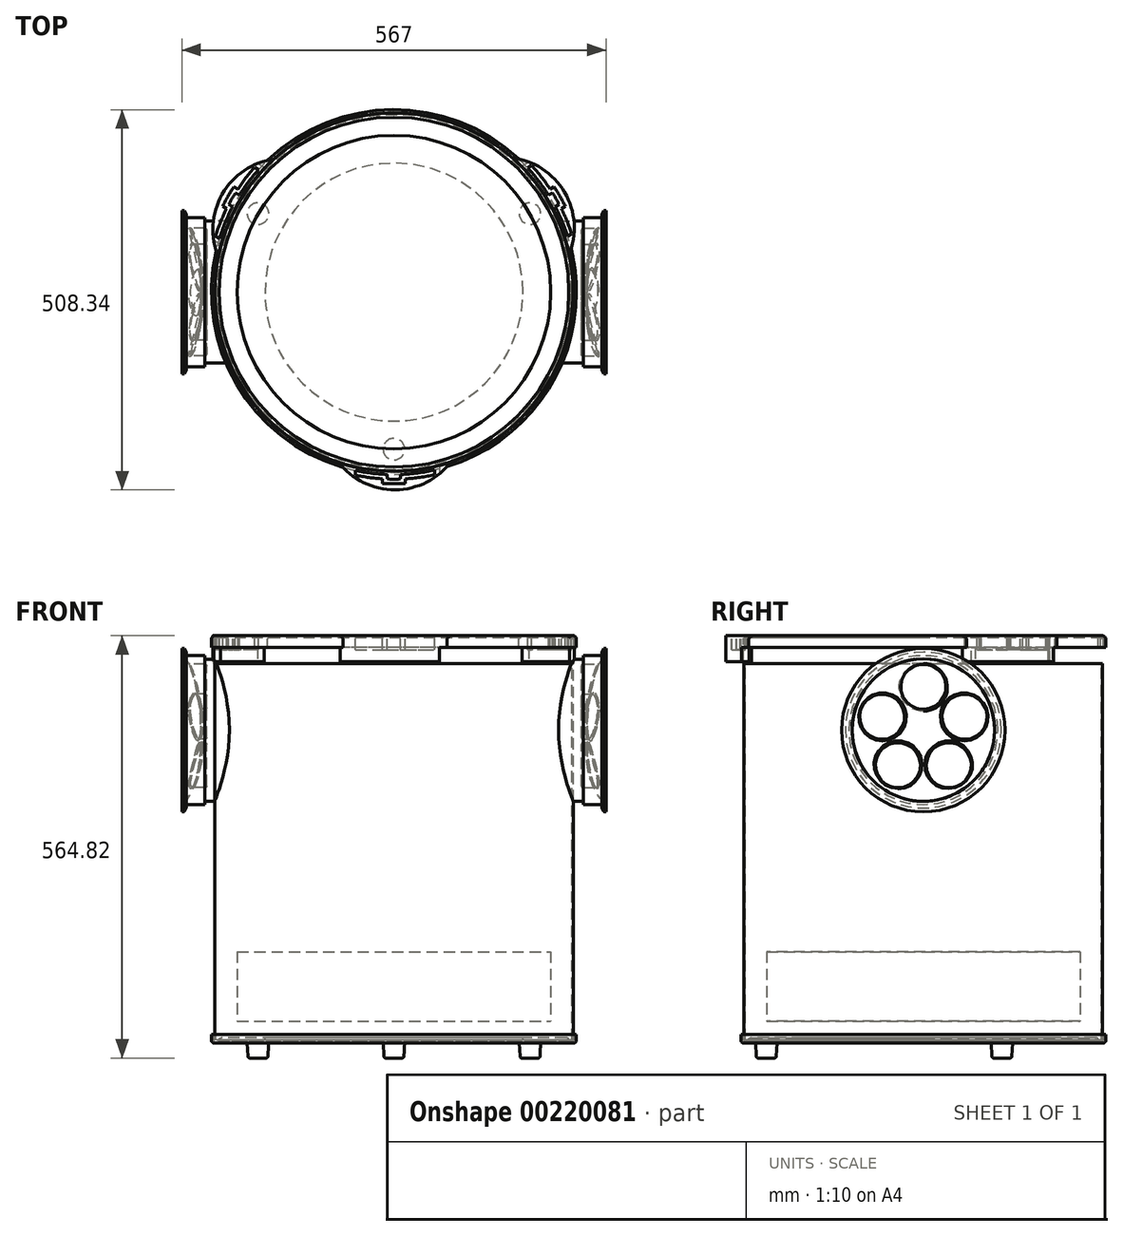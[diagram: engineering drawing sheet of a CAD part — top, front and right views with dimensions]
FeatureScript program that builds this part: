
annotation { "Feature Type Name" : "Feature", "Feature Type Description" : "" }
export const myFeature = defineFeature(function(context is Context, id is Id, definition is map)
    precondition{}
    {
        {
            var Q0;
            Q0=qCreatedBy(makeId("Front.planeOp"),FACE);
            var sketch = newSketch(context, id + "F0", { "sketchPlane" : qUnion([Q0])});
            skLineSegment(sketch, "E0", {"start": v(0, 0) * mm, "end": v(266.4, 0) * mm, "construction": true});
            skArc(sketch, "E1", {"start": v(244, 0) * mm, "mid": v(238.93, 5.08) * mm, "end": v(233.85, 0) * mm});
            skLineSegment(sketch, "E2", {"start": v(233.85, 0) * mm, "end": v(233.85, -10.92) * mm});
            skLineSegment(sketch, "E3", {"start": v(244, 0) * mm, "end": v(244, -10.92) * mm});
            skArc(sketch, "E4", {"start": v(240.83, 0) * mm, "mid": v(238.93, 1.9) * mm, "end": v(237.02, 0) * mm});
            skLineSegment(sketch, "E5", {"start": v(237.02, 0) * mm, "end": v(237.02, -10.92) * mm});
            skLineSegment(sketch, "E6", {"start": v(240.83, 0) * mm, "end": v(240.83, -10.92) * mm});
            skLineSegment(sketch, "E7", {"start": v(233.85, -10.92) * mm, "end": v(237.02, -10.92) * mm});
            skLineSegment(sketch, "E8.trimOffspring", {"start": v(240.83, -10.92) * mm, "end": v(244, -10.92) * mm});
            skLineSegment(sketch, "E9", {"start": v(239.69, 0) * mm, "end": v(239.69, -535.86) * mm});
            skLineSegment(sketch, "E10", {"start": v(238.16, 0) * mm, "end": v(238.16, -535.86) * mm});
            skLineSegment(sketch, "E11", {"start": v(238.16, 0) * mm, "end": v(239.69, 0) * mm});
            skLineSegment(sketch, "E12", {"start": v(-59.24, -539.93) * mm, "end": v(313.45, -539.93) * mm, "construction": true});
            skLineSegment(sketch, "E13", {"start": v(244, -528.24) * mm, "end": v(244, -535.86) * mm});
            skLineSegment(sketch, "E14", {"start": v(0, 0) * mm, "end": v(0, -616.75) * mm, "construction": true});
            skLineSegment(sketch, "E15", {"start": v(240.83, -528.24) * mm, "end": v(244, -528.24) * mm});
            skLineSegment(sketch, "E16", {"start": v(240.83, -528.24) * mm, "end": v(240.83, -536) * mm});
            skLineSegment(sketch, "E17", {"start": v(235.18, -536.75) * mm, "end": v(240.07, -536.75) * mm});
            skLineSegment(sketch, "E18", {"start": v(230.42, -532.69) * mm, "end": v(172.5, -532.69) * mm});
            skLineSegment(sketch, "E19", {"start": v(172.5, -535.86) * mm, "end": v(230.6, -535.86) * mm});
            skLineSegment(sketch, "E20", {"start": v(235.37, -539.93) * mm, "end": v(239.94, -539.93) * mm});
            skLineSegment(sketch, "E21", {"start": v(238.16, -535.86) * mm, "end": v(239.69, -535.86) * mm});
            skLineSegment(sketch, "E22", {"start": v(172.5, -532.69) * mm, "end": v(172.5, -535.86) * mm});
            skArc(sketch, "E23.filletArc", {"start": v(231.36, -536.5) * mm, "mid": v(232.73, -538.96) * mm, "end": v(235.37, -539.93) * mm});
            skPoint(sketch, "E24.visualSharp", {"position": v(244, -539.93) * mm});
            skArc(sketch, "E24.filletArc", {"start": v(239.94, -539.93) * mm, "mid": v(242.81, -538.74) * mm, "end": v(244, -535.86) * mm});
            skPoint(sketch, "E25.visualSharp", {"position": v(231.3, -535.86) * mm});
            skPoint(sketch, "E26.visualSharp", {"position": v(234.48, -532.69) * mm});
            skArc(sketch, "E26.filletArc", {"start": v(234.43, -536.11) * mm, "mid": v(233.05, -533.66) * mm, "end": v(230.42, -532.69) * mm});
            skPoint(sketch, "E27.visualSharp", {"position": v(234.48, -536.75) * mm});
            skPoint(sketch, "E28.visualSharp", {"position": v(240.83, -536.75) * mm});
            skArc(sketch, "E28.filletArc", {"start": v(240.07, -536.75) * mm, "mid": v(240.6, -536.53) * mm, "end": v(240.83, -536) * mm});
            skArc(sketch, "E29.filletArc", {"start": v(231.36, -536.5) * mm, "mid": v(231.1, -536.05) * mm, "end": v(230.6, -535.86) * mm});
            skArc(sketch, "E30.filletArc", {"start": v(234.43, -536.11) * mm, "mid": v(234.69, -536.57) * mm, "end": v(235.18, -536.75) * mm});
            skPoint(sketch, "E31", {"position": v(238.93, 5.08) * mm});
            skSolve(sketch);
        }
        {
            var Q0;
            Q0=qCreatedBy(makeId("Front.planeOp"),FACE);
            var sketch = newSketch(context, id + "F1", { "sketchPlane" : qUnion([Q0])});
            skLineSegment(sketch, "E32", {"start": v(0, 0) * mm, "end": v(0, -692.69) * mm, "construction": true});
            skSolve(sketch);
        }
        {
            var Q0;
            Q0 = qSketchRegion(id + "F0", true);
            var Q1;
            Q1 = qConstructionFilter(qBodyType(qCreatedBy(id + "F0" ,EDGE), BodyType.WIRE), ConstructionObject.NO);
            var Q2;
            Q2=sQuery(id+"F1.wireOp",EDGE,"E32");
            revolve(context, id + "F2", {"entities" : qUnion([Q0]), "surfaceEntities" : qUnion([Q1]), "axis" : qUnion([Q2]), "revolveType" : RevolveType.FULL});
        }
        {
            var Q0;
            Q0=qCreatedBy(makeId("Right.planeOp"),FACE);
            cPlane(context, id + "F3", {"entities" : qUnion([Q0]), "cplaneType" : CPlaneType.OFFSET, "offset" : 283.5 * mm, "width" : 152.4 * mm, "height" : 152.4 * mm});
        }
        {
            var Q0;
            Q0=qCreatedBy(id+"F3.planeOp",FACE);
            cPlane(context, id + "F4", {"entities" : qUnion([Q0]), "cplaneType" : CPlaneType.OFFSET, "offset" : 5.6 * mm, "oppositeDirection" : true, "width" : 152.4 * mm, "height" : 152.4 * mm});
        }
        {
            var Q0;
            Q0=qCreatedBy(id+"F4.planeOp",FACE);
            cPlane(context, id + "F5", {"entities" : qUnion([Q0]), "cplaneType" : CPlaneType.OFFSET, "offset" : 24.76 * mm, "oppositeDirection" : true, "width" : 152.4 * mm, "height" : 152.4 * mm});
        }
        {
            var Q0;
            Q0=qCreatedBy(id+"F3.planeOp",FACE);
            var sketch = newSketch(context, id + "F6", { "sketchPlane" : qUnion([Q0])});
            skLineSegment(sketch, "E33", {"start": v(0, 0) * mm, "end": v(0, -1376.22) * mm, "construction": true});
            skCircle(sketch, "E34", {"center": v(0, -121.28) * mm, "radius": 109.22 * mm});
            skCircle(sketch, "E35", {"center": v(0, -121.28) * mm, "radius": 99.57 * mm});
            skCircle(sketch, "E36", {"center": v(0, -121.28) * mm, "radius": 95 * mm});
            skLineSegment(sketch, "E37", {"start": v(-238.93, 5.08) * mm, "end": v(238.93, 5.08) * mm, "construction": true});
            skSolve(sketch);
        }
        {
            var Q0;
            Q0=makeQuery(id+"F6.imprint","IMPRINT",FACE,{"disambiguationData":[TD([[makeQuery(id+"F6.imprint","IMPRINT",EDGE,{"derivedFrom":sQuery(id+"F6.wireOp",EDGE,"E36")}),1.0]])]});
            var Q1;
            Q1=sQuery(id+"F6.wireOp",EDGE,"E37");
            var Q2;
            Q2=sQuery(id+"F6.wireOp",EDGE,"E36");
            var Q3;
            Q3=makeQuery(id+"F2.opRevolve","SWEPT_FACE",FACE,{"disambiguationData":[OSD([sQuery(id+"F0.wireOp",EDGE,"E9")])]});
            extrude(context, id + "F7", {"entities" : qUnion([Q0]), "surfaceEntities" : qUnion([Q1, Q2]), "endBound" : BoundingType.UP_TO_SURFACE, "oppositeDirection" : true, "endBoundEntityFace" : qUnion([Q3]), "depth" : 25.4 * mm});
        }
        {
            var Q0;
            Q0=makeQuery(id+"F6.imprint","IMPRINT",FACE,{"disambiguationData":[TD([[makeQuery(id+"F6.imprint","IMPRINT",EDGE,{"derivedFrom":sQuery(id+"F6.wireOp",EDGE,"E35")}),1.0]])]});
            var Q1;
            Q1=qCreatedBy(id+"F5.planeOp",FACE);
            extrude(context, id + "F8", {"entities" : qUnion([Q0]), "operationType" : NewBodyOperationType.ADD, "endBound" : BoundingType.UP_TO_SURFACE, "oppositeDirection" : true, "endBoundEntityFace" : qUnion([Q1]), "depth" : 25.4 * mm});
        }
        {
            var Q0;
            Q0=makeQuery(id+"F6.imprint","IMPRINT",FACE,{"disambiguationData":[TD([[makeQuery(id+"F6.imprint","IMPRINT",EDGE,{"derivedFrom":sQuery(id+"F6.wireOp",EDGE,"E34")}),1.0]])]});
            var Q1;
            Q1=qCreatedBy(id+"F4.planeOp",FACE);
            extrude(context, id + "F9", {"entities" : qUnion([Q0]), "operationType" : NewBodyOperationType.ADD, "endBound" : BoundingType.UP_TO_SURFACE, "oppositeDirection" : true, "endBoundEntityFace" : qUnion([Q1]), "depth" : 25.4 * mm});
        }
        {
            var Q0;
            Q0=qCreatedBy(makeId("Front.planeOp"),FACE);
            var sketch = newSketch(context, id + "F10", { "sketchPlane" : qUnion([Q0])});
            skLineSegment(sketch, "E38.0", {"start": v(283.5, -12.06) * mm, "end": v(283.5, -26.03) * mm, "construction": true});
            skPoint(sketch, "E39", {"position": v(283.5, -26.03) * mm});
            skPoint(sketch, "E40.orphan", {"position": v(283.5, -121.28) * mm});
            skPoint(sketch, "E41", {"position": v(257.34, -121.28) * mm});
            skEllipticalArc(sketch, "E42", {});
            skLineSegment(sketch, "E43", {"start": v(283.5, -26.03) * mm, "end": v(283.5, -121.28) * mm});
            skLineSegment(sketch, "E44", {"start": v(283.5, -121.28) * mm, "end": v(257.34, -121.28) * mm});
            skPoint(sketch, "E45.trimOffspring.end.orphan", {"position": v(283.5, -230.5) * mm});
            const initialGuessF10  = {"E42": [0.28350210000000003, -0.121285, 0, 1, 0.09525, 0.026162, 0, 1.5707963267948966]};
            skSetInitialGuess(sketch, initialGuessF10);
            skSolve(sketch);
        }
        {
            var Q0;
            Q0 = qSketchRegion(id + "F10", true);
            var Q1;
            Q1=makeQuery(id+"F7.opExtrude","SWEPT_FACE",FACE,{"disambiguationData":[OSD([sQuery(id+"F6.wireOp",EDGE,"E36")])]});
            revolve(context, id + "F11", {"operationType" : NewBodyOperationType.REMOVE, "entities" : qUnion([Q0]), "axis" : qUnion([Q1]), "revolveType" : RevolveType.FULL, "oppositeDirection" : true});
        }
        {
            var Q0;
            Q0=qCreatedBy(id+"F3.planeOp",FACE);
            var sketch = newSketch(context, id + "F12", { "sketchPlane" : qUnion([Q0])});
            skCircle(sketch, "E46.0", {"center": v(0, -121.28) * mm, "radius": 95.25 * mm, "construction": true});
            skLineSegment(sketch, "E47", {"start": v(0, -121.28) * mm, "end": v(0, 34.17) * mm, "construction": true});
            skCircle(sketch, "E48", {"center": v(0, -63.3) * mm, "radius": 30.16 * mm});
            skCircle(sketch, "E49.0", {"center": v(0, -121.28) * mm, "radius": 109.22 * mm, "construction": true});
            skCircle(sketch, "E50.1.0", {"center": v(-55.14, -103.37) * mm, "radius": 30.16 * mm});
            skCircle(sketch, "E50.2.0", {"center": v(-34.08, -168.19) * mm, "radius": 30.16 * mm});
            skCircle(sketch, "E50.3.0", {"center": v(34.08, -168.19) * mm, "radius": 30.16 * mm});
            skCircle(sketch, "E50.4.0", {"center": v(55.14, -103.37) * mm, "radius": 30.16 * mm});
            skSolve(sketch);
        }
        {
            var Q0;
            Q0 = qSketchRegion(id + "F12", true);
            extrude(context, id + "F13", {"entities" : qUnion([Q0]), "operationType" : NewBodyOperationType.REMOVE, "oppositeDirection" : true, "depth" : 33.02 * mm});
        }
        {
            var Q0;
            Q0=makeQuery(id+"F13.boolean.opBoolean","COPY",EDGE,{"derivedFrom":makeQuery(id+"F13.opExtrude","CAP_EDGE",EDGE,{"disambiguationData":[OSD([sQuery(id+"F12.wireOp",EDGE,"E50.3.0")])],"isStart":false})});
            var Q1;
            Q1=makeQuery(id+"F13.boolean.opBoolean","COPY",EDGE,{"derivedFrom":makeQuery(id+"F13.opExtrude","CAP_EDGE",EDGE,{"disambiguationData":[OSD([sQuery(id+"F12.wireOp",EDGE,"E50.4.0")])],"isStart":false})});
            var Q2;
            Q2=makeQuery(id+"F13.boolean.opBoolean","COPY",FACE,{"derivedFrom":makeQuery(id+"F13.opExtrude","SWEPT_FACE",FACE,{"disambiguationData":[OSD([sQuery(id+"F12.wireOp",EDGE,"E48")])]})});
            var Q3;
            Q3=makeQuery(id+"F13.boolean.opBoolean","COPY",EDGE,{"derivedFrom":makeQuery(id+"F13.opExtrude","CAP_EDGE",EDGE,{"disambiguationData":[OSD([sQuery(id+"F12.wireOp",EDGE,"E50.1.0")])],"isStart":false})});
            var Q4;
            Q4=makeQuery(id+"F13.boolean.opBoolean","COPY",EDGE,{"derivedFrom":makeQuery(id+"F13.opExtrude","CAP_EDGE",EDGE,{"disambiguationData":[OSD([sQuery(id+"F12.wireOp",EDGE,"E50.2.0")])],"isStart":false})});
            var Q5;
            Q5=makeQuery(id+"F13.boolean.opBoolean","INTERSECT",EDGE,{"derivedFrom":[makeQuery(id+"F11.boolean.opBoolean","COPY",FACE,{"derivedFrom":makeQuery(id+"F11.opRevolve","SWEPT_FACE",FACE,{"disambiguationData":[OSD([sQuery(id+"F10.wireOp",EDGE,"E42")])]})}),makeQuery(id+"F13.opExtrude","SWEPT_FACE",FACE,{"disambiguationData":[OSD([sQuery(id+"F12.wireOp",EDGE,"E50.4.0")])]})]});
            var Q6;
            Q6=makeQuery(id+"F13.boolean.opBoolean","INTERSECT",EDGE,{"derivedFrom":[makeQuery(id+"F11.boolean.opBoolean","COPY",FACE,{"derivedFrom":makeQuery(id+"F11.opRevolve","SWEPT_FACE",FACE,{"disambiguationData":[OSD([sQuery(id+"F10.wireOp",EDGE,"E42")])]})}),makeQuery(id+"F13.opExtrude","SWEPT_FACE",FACE,{"disambiguationData":[OSD([sQuery(id+"F12.wireOp",EDGE,"E50.3.0")])]})]});
            var Q7;
            Q7=makeQuery(id+"F13.boolean.opBoolean","INTERSECT",EDGE,{"derivedFrom":[makeQuery(id+"F11.boolean.opBoolean","COPY",FACE,{"derivedFrom":makeQuery(id+"F11.opRevolve","SWEPT_FACE",FACE,{"disambiguationData":[OSD([sQuery(id+"F10.wireOp",EDGE,"E42")])]})}),makeQuery(id+"F13.opExtrude","SWEPT_FACE",FACE,{"disambiguationData":[OSD([sQuery(id+"F12.wireOp",EDGE,"E50.2.0")])]})]});
            var Q8;
            Q8=makeQuery(id+"F13.boolean.opBoolean","INTERSECT",EDGE,{"derivedFrom":[makeQuery(id+"F11.boolean.opBoolean","COPY",FACE,{"derivedFrom":makeQuery(id+"F11.opRevolve","SWEPT_FACE",FACE,{"disambiguationData":[OSD([sQuery(id+"F10.wireOp",EDGE,"E42")])]})}),makeQuery(id+"F13.opExtrude","SWEPT_FACE",FACE,{"disambiguationData":[OSD([sQuery(id+"F12.wireOp",EDGE,"E50.1.0")])]})]});
            var Q9;
            Q9=makeQuery(id+"F11.boolean.opBoolean","COPY",EDGE,{"derivedFrom":makeQuery(id+"F11.opRevolve","SWEPT_EDGE",EDGE,{"disambiguationData":[OSD([sQuery(id+"F10.wireOp",EDGE,"E42"),sQuery(id+"F10.wireOp",EDGE,"E43")])]})});
            fillet(context, id + "F14", {"entities" : qUnion([Q0, Q1, Q2, Q3, Q4, Q5, Q6, Q7, Q8, Q9]), "radius" : 2.3 * mm, "tangentPropagation" : true, "allowEdgeOverflow" : false});
        }
        {
            var Q0;
            Q0=qCreatedBy(makeId("Front.planeOp"),FACE);
            var sketch = newSketch(context, id + "F15", { "sketchPlane" : qUnion([Q0])});
            skLineSegment(sketch, "E51.0", {"start": v(277.91, -17.14) * mm, "end": v(277.91, -12.06) * mm});
            skLineSegment(sketch, "E52", {"start": v(277.91, -17.14) * mm, "end": v(280.45, -12.06) * mm});
            skLineSegment(sketch, "E53", {"start": v(277.91, -12.06) * mm, "end": v(280.45, -12.06) * mm});
            skPoint(sketch, "E54.orphan", {"position": v(277.91, -230.5) * mm});
            skSolve(sketch);
        }
        {
            var Q0;
            Q0 = qSketchRegion(id + "F15", true);
            var Q1;
            Q1=makeQuery(id+"F9.opExtrude","SWEPT_FACE",FACE,{"disambiguationData":[OSD([sQuery(id+"F6.wireOp",EDGE,"E34")])]});
            revolve(context, id + "F16", {"operationType" : NewBodyOperationType.REMOVE, "entities" : qUnion([Q0]), "axis" : qUnion([Q1]), "revolveType" : RevolveType.FULL, "oppositeDirection" : true});
        }
        {
            var Q0;
            Q0=makeQuery(id+"F7.opExtrude","SWEPT_BODY",BODY,{"disambiguationData":[OSD([sQuery(id+"F6.wireOp",EDGE,"E36")])]});
            var Q1;
            Q1=qCreatedBy(makeId("Right.planeOp"),FACE);
            mirror(context, id + "F17", {"entities" : qUnion([Q0]), "mirrorPlane" : qUnion([Q1])});
        }
        {
            var Q0;
            Q0=makeQuery(id+"F2.opRevolve","SWEPT_FACE",FACE,{"disambiguationData":[OSD([sQuery(id+"F0.wireOp",EDGE,"E19")])]});
            cPlane(context, id + "F18", {"entities" : qUnion([Q0]), "cplaneType" : CPlaneType.OFFSET, "offset" : 25.4 * mm, "oppositeDirection" : true, "width" : 152.4 * mm, "height" : 152.4 * mm});
        }
        {
            var Q0;
            Q0=qCreatedBy(id+"F18.planeOp",FACE);
            var sketch = newSketch(context, id + "F19", { "sketchPlane" : qUnion([Q0])});
            skCircle(sketch, "E55.0", {"center": v(0, 0) * mm, "radius": 172.5 * mm, "construction": true});
            skCircle(sketch, "E56", {"center": v(0, 0) * mm, "radius": 209.55 * mm});
            skSolve(sketch);
        }
        {
            var Q0;
            Q0 = qSketchRegion(id + "F19", true);
            extrude(context, id + "F20", {"entities" : qUnion([Q0]), "oppositeDirection" : true, "depth" : 92.96 * mm});
        }
        {
            var Q0;
            Q0=makeQuery(id+"F2.opRevolve","SWEPT_FACE",FACE,{"disambiguationData":[OSD([sQuery(id+"F0.wireOp",EDGE,"E19")])]});
            var sketch = newSketch(context, id + "F21", { "sketchPlane" : qUnion([Q0])});
            skCircle(sketch, "E57.0", {"center": v(0, 0) * mm, "radius": 244 * mm, "construction": true});
            skCircle(sketch, "E58", {"center": v(0, 0) * mm, "radius": 209.97 * mm, "construction": true});
            skCircle(sketch, "E59", {"center": v(0, 209.97) * mm, "radius": 14.48 * mm});
            skCircle(sketch, "E60.1.0", {"center": v(-181.84, -104.98) * mm, "radius": 14.48 * mm});
            skCircle(sketch, "E60.2.0", {"center": v(181.84, -104.98) * mm, "radius": 14.48 * mm});
            skSolve(sketch);
        }
        {
            var Q0;
            Q0 = qSketchRegion(id + "F21", true);
            extrude(context, id + "F22", {"entities" : qUnion([Q0]), "operationType" : NewBodyOperationType.ADD, "depth" : 23.88 * mm, "hasDraft" : true, "draftAngle" : 3 * degree, "draftPullDirection" : true});
        }
        {
            var Q0;
            Q0=makeQuery(id+"F22.opExtrude","CAP_EDGE",EDGE,{"disambiguationData":[OSD([sQuery(id+"F21.wireOp",EDGE,"E59")])],"isStart":false});
            var Q1;
            Q1=makeQuery(id+"F22.opExtrude","CAP_EDGE",EDGE,{"disambiguationData":[OSD([sQuery(id+"F21.wireOp",EDGE,"E60.1.0")])],"isStart":false});
            var Q2;
            Q2=makeQuery(id+"F22.opExtrude","CAP_EDGE",EDGE,{"disambiguationData":[OSD([sQuery(id+"F21.wireOp",EDGE,"E60.2.0")])],"isStart":false});
            fillet(context, id + "F23", {"entities" : qUnion([Q0, Q1, Q2]), "radius" : 2.3 * mm, "tangentPropagation" : true, "allowEdgeOverflow" : false});
        }
        {
            var Q0;
            Q0=qCreatedBy(makeId("Top.planeOp"),FACE);
            cPlane(context, id + "F24", {"entities" : qUnion([Q0]), "cplaneType" : CPlaneType.OFFSET, "offset" : 5.08 * mm, "width" : 152.4 * mm, "height" : 152.4 * mm});
        }
        {
            var Q0;
            Q0=qCreatedBy(id+"F24.planeOp",FACE);
            var sketch = newSketch(context, id + "F25", { "sketchPlane" : qUnion([Q0])});
            skCircle(sketch, "E61.0", {"center": v(0, 0) * mm, "radius": 244 * mm, "construction": true});
            skLineSegment(sketch, "E62", {"start": v(0, 0) * mm, "end": v(0, -355.56) * mm, "construction": true});
            skArc(sketch, "E63", {"start": v(-74.28, -227.08) * mm, "mid": v(1.49, -238.92) * mm, "end": v(77.1, -226.14) * mm});
            skLineSegment(sketch, "E64", {"start": v(-74.28, -176.06) * mm, "end": v(-74.28, -268.16) * mm, "construction": true});
            skLineSegment(sketch, "E65", {"start": v(77.1, -171.77) * mm, "end": v(77.1, -259.18) * mm, "construction": true});
            skPoint(sketch, "E66", {"position": v(0, -264.33) * mm});
            skCircle(sketch, "E67.0", {"center": v(0, 0) * mm, "radius": 233.85 * mm, "construction": true});
            skPoint(sketch, "E68", {"position": v(-74.28, -227.08) * mm});
            skPoint(sketch, "E69", {"position": v(77.1, -226.14) * mm});
            skArc(sketch, "E70", {"start": v(-74.28, -227.08) * mm, "mid": v(1.64, -264.33) * mm, "end": v(77.1, -226.14) * mm});
            skArc(sketch, "E71.1.0", {"start": v(233.8, 49.21) * mm, "mid": v(206.17, 120.75) * mm, "end": v(157.3, 179.84) * mm});
            skArc(sketch, "E71.1.1", {"start": v(233.8, 49.21) * mm, "mid": v(228.1, 133.59) * mm, "end": v(157.3, 179.84) * mm});
            skArc(sketch, "E71.2.0", {"start": v(-159.52, 177.87) * mm, "mid": v(-207.65, 118.17) * mm, "end": v(-234.4, 46.3) * mm});
            skArc(sketch, "E71.2.1", {"start": v(-159.52, 177.87) * mm, "mid": v(-229.74, 130.74) * mm, "end": v(-234.4, 46.3) * mm});
            skSolve(sketch);
        }
        {
            var Q0;
            Q0 = qSketchRegion(id + "F25", true);
            var Q1;
            Q1=makeQuery(id+"F2.opRevolve","SWEPT_FACE",FACE,{"disambiguationData":[OSD([sQuery(id+"F0.wireOp",EDGE,"E8.trimOffspring")])]});
            extrude(context, id + "F26", {"entities" : qUnion([Q0]), "operationType" : NewBodyOperationType.ADD, "oppositeDirection" : true, "endBoundEntityFace" : qUnion([Q1]), "depth" : 35.05 * mm});
        }
        {
            var Q0;
            Q0=makeQuery(id+"F26.opExtrude","CAP_FACE",FACE,{"disambiguationData":[OSD([sQuery(id+"F25.wireOp",EDGE,"E71.2.0"),sQuery(id+"F25.wireOp",EDGE,"E71.2.1")])],"isStart":false});
            var sketch = newSketch(context, id + "F27", { "sketchPlane" : qUnion([Q0])});
            skArc(sketch, "E72.0", {"start": v(-159.52, -177.87) * mm, "mid": v(-171.17, -175.61) * mm, "end": v(-182.44, -171.92) * mm});
            skArc(sketch, "E73.0", {"start": v(-159.52, -177.87) * mm, "mid": v(-165.82, -172.01) * mm, "end": v(-171.91, -165.93) * mm});
            skLineSegment(sketch, "E74", {"start": v(-147.33, -83.85) * mm, "end": v(-229.74, -130.74) * mm, "construction": true});
            skLineSegment(sketch, "E75", {"start": v(-171.91, -165.93) * mm, "end": v(-182.44, -171.92) * mm});
            skLineSegment(sketch, "E76", {"start": v(-230.45, -63.05) * mm, "end": v(-240.99, -69.05) * mm});
            skArc(sketch, "E77.trimOffspring", {"start": v(-240.99, -69.05) * mm, "mid": v(-238.4, -57.47) * mm, "end": v(-234.4, -46.3) * mm});
            skArc(sketch, "E78.trimOffspring", {"start": v(-230.45, -63.05) * mm, "mid": v(-232.58, -54.71) * mm, "end": v(-234.4, -46.3) * mm});
            skPoint(sketch, "E79.orphan", {"position": v(-213.52, -189.6) * mm});
            skArc(sketch, "E80.1.0", {"start": v(233.8, -49.21) * mm, "mid": v(237.67, -60.43) * mm, "end": v(240.1, -72.04) * mm});
            skArc(sketch, "E80.1.1", {"start": v(233.8, -49.21) * mm, "mid": v(231.88, -57.6) * mm, "end": v(229.65, -65.92) * mm});
            skLineSegment(sketch, "E80.1.2", {"start": v(229.65, -65.92) * mm, "end": v(240.1, -72.04) * mm});
            skLineSegment(sketch, "E80.1.3", {"start": v(169.83, -168.05) * mm, "end": v(180.29, -174.18) * mm});
            skArc(sketch, "E80.1.4", {"start": v(180.29, -174.18) * mm, "mid": v(168.97, -177.73) * mm, "end": v(157.3, -179.84) * mm});
            skArc(sketch, "E80.1.5", {"start": v(169.83, -168.05) * mm, "mid": v(163.67, -174.06) * mm, "end": v(157.3, -179.84) * mm});
            skArc(sketch, "E80.2.0", {"start": v(-74.28, 227.08) * mm, "mid": v(-66.5, 236.04) * mm, "end": v(-57.67, 243.96) * mm});
            skArc(sketch, "E80.2.1", {"start": v(-74.28, 227.08) * mm, "mid": v(-66.05, 229.61) * mm, "end": v(-57.74, 231.84) * mm});
            skLineSegment(sketch, "E80.2.2", {"start": v(-57.74, 231.84) * mm, "end": v(-57.67, 243.96) * mm});
            skLineSegment(sketch, "E80.2.3", {"start": v(60.62, 231.1) * mm, "end": v(60.7, 243.22) * mm});
            skArc(sketch, "E80.2.4", {"start": v(60.7, 243.22) * mm, "mid": v(69.43, 235.2) * mm, "end": v(77.1, 226.14) * mm});
            skArc(sketch, "E80.2.5", {"start": v(60.62, 231.1) * mm, "mid": v(68.9, 228.77) * mm, "end": v(77.1, 226.14) * mm});
            skSolve(sketch);
        }
        {
            var Q0;
            Q0=makeQuery(id+"F27.imprint","IMPRINT",FACE,{"disambiguationData":[TD([[makeQuery(id+"F27.imprint","IMPRINT",EDGE,{"derivedFrom":sQuery(id+"F27.wireOp",EDGE,"E72.0")}),-1.0]])]});
            var Q1;
            Q1=makeQuery(id+"F27.imprint","IMPRINT",FACE,{"disambiguationData":[TD([[makeQuery(id+"F27.imprint","IMPRINT",EDGE,{"derivedFrom":sQuery(id+"F27.wireOp",EDGE,"E76")}),-1.0]])]});
            var Q2;
            Q2=makeQuery(id+"F27.imprint","IMPRINT",FACE,{"disambiguationData":[TD([[makeQuery(id+"F27.imprint","IMPRINT",EDGE,{"derivedFrom":sQuery(id+"F27.wireOp",EDGE,"E80.1.3")}),-1.0]])]});
            var Q3;
            Q3=makeQuery(id+"F27.imprint","IMPRINT",FACE,{"disambiguationData":[TD([[makeQuery(id+"F27.imprint","IMPRINT",EDGE,{"derivedFrom":sQuery(id+"F27.wireOp",EDGE,"E80.1.0")}),-1.0]])]});
            var Q4;
            Q4=makeQuery(id+"F27.imprint","IMPRINT",FACE,{"disambiguationData":[TD([[makeQuery(id+"F27.imprint","IMPRINT",EDGE,{"derivedFrom":sQuery(id+"F27.wireOp",EDGE,"E80.2.0")}),-1.0]])]});
            var Q5;
            Q5=makeQuery(id+"F27.imprint","IMPRINT",FACE,{"disambiguationData":[TD([[makeQuery(id+"F27.imprint","IMPRINT",EDGE,{"derivedFrom":sQuery(id+"F27.wireOp",EDGE,"E80.2.3")}),-1.0]])]});
            var Q6;
            Q6=makeQuery(id+"F26.boolean.opBoolean","SPLIT",FACE,{"disambiguationData":[TD([makeQuery(id+"F2.opRevolve","SWEPT_FACE",FACE,{"disambiguationData":[OSD([sQuery(id+"F0.wireOp",EDGE,"E3")])]}),makeQuery(id+"F2.opRevolve","SWEPT_FACE",FACE,{"disambiguationData":[OSD([sQuery(id+"F0.wireOp",EDGE,"E6")])]}),makeQuery(id+"F26.opExtrude","SWEPT_FACE",FACE,{"disambiguationData":[OSD([sQuery(id+"F25.wireOp",EDGE,"E71.1.1")])]}),makeQuery(id+"F26.opExtrude","SWEPT_FACE",FACE,{"disambiguationData":[OSD([sQuery(id+"F25.wireOp",EDGE,"E71.2.1")])]})])],"derivedFrom":makeQuery(id+"F2.opRevolve","SWEPT_FACE",FACE,{"disambiguationData":[OSD([sQuery(id+"F0.wireOp",EDGE,"E8.trimOffspring")])]})});
            extrude(context, id + "F28", {"entities" : qUnion([Q0, Q1, Q2, Q3, Q4, Q5]), "operationType" : NewBodyOperationType.REMOVE, "endBound" : BoundingType.UP_TO_SURFACE, "oppositeDirection" : true, "endBoundEntityFace" : qUnion([Q6]), "depth" : 25.4 * mm});
        }
        {
            var Q0;
            Q0=makeQuery(id+"F28.boolean.opBoolean","COPY",EDGE,{"derivedFrom":makeQuery(id+"F28.opExtrude","CAP_EDGE",EDGE,{"disambiguationData":[OSD([sQuery(id+"F27.wireOp",EDGE,"E80.1.3")])],"isStart":true})});
            var Q1;
            Q1=makeQuery(id+"F28.boolean.opBoolean","COPY",EDGE,{"derivedFrom":makeQuery(id+"F28.opExtrude","CAP_EDGE",EDGE,{"disambiguationData":[OSD([sQuery(id+"F27.wireOp",EDGE,"E80.1.2")])],"isStart":true})});
            var Q2;
            Q2=makeQuery(id+"F28.boolean.opBoolean","COPY",EDGE,{"derivedFrom":makeQuery(id+"F28.opExtrude","CAP_EDGE",EDGE,{"disambiguationData":[OSD([sQuery(id+"F27.wireOp",EDGE,"E75")])],"isStart":true})});
            var Q3;
            Q3=makeQuery(id+"F28.boolean.opBoolean","COPY",EDGE,{"derivedFrom":makeQuery(id+"F28.opExtrude","CAP_EDGE",EDGE,{"disambiguationData":[OSD([sQuery(id+"F27.wireOp",EDGE,"E76")])],"isStart":true})});
            var Q4;
            Q4=makeQuery(id+"F28.boolean.opBoolean","COPY",EDGE,{"derivedFrom":makeQuery(id+"F28.opExtrude","CAP_EDGE",EDGE,{"disambiguationData":[OSD([sQuery(id+"F27.wireOp",EDGE,"E80.2.3")])],"isStart":true})});
            var Q5;
            Q5=makeQuery(id+"F28.boolean.opBoolean","COPY",EDGE,{"derivedFrom":makeQuery(id+"F28.opExtrude","CAP_EDGE",EDGE,{"disambiguationData":[OSD([sQuery(id+"F27.wireOp",EDGE,"E80.2.2")])],"isStart":true})});
            chamfer(context, id + "F29", {"entities" : qUnion([Q0, Q1, Q2, Q3, Q4, Q5]), "width" : 19.05 * mm, "tangentPropagation" : true});
        }
        {
            var Q0;
            Q0=makeQuery(id+"F26.opExtrude","CAP_FACE",FACE,{"disambiguationData":[OSD([sQuery(id+"F25.wireOp",EDGE,"E63"),sQuery(id+"F25.wireOp",EDGE,"E70")])],"isStart":true});
            var sketch = newSketch(context, id + "F30", { "sketchPlane" : qUnion([Q0])});
            skArc(sketch, "E81.0", {"start": v(-74.28, -227.08) * mm, "mid": v(1.49, -238.92) * mm, "end": v(77.1, -226.14) * mm, "construction": true});
            skArc(sketch, "E82", {"start": v(-51.48, -238.51) * mm, "mid": v(-30.37, -242.1) * mm, "end": v(-9.02, -243.84) * mm});
            skArc(sketch, "E83", {"start": v(-51.44, -244.75) * mm, "mid": v(-33.37, -247.87) * mm, "end": v(-15.11, -249.64) * mm});
            skLineSegment(sketch, "E84", {"start": v(-51.48, -238.51) * mm, "end": v(-51.44, -244.75) * mm});
            skLineSegment(sketch, "E85", {"start": v(54.43, -237.86) * mm, "end": v(54.47, -244.1) * mm});
            skLineSegment(sketch, "E86", {"start": v(0, 0) * mm, "end": v(0, -323.03) * mm, "construction": true});
            skLineSegment(sketch, "E87", {"start": v(-15.11, -255.75) * mm, "end": v(-15.11, -249.64) * mm});
            skLineSegment(sketch, "E88", {"start": v(15.11, -255.75) * mm, "end": v(15.11, -249.64) * mm});
            skArc(sketch, "E89", {"start": v(-15.11, -255.75) * mm, "mid": v(0, -256.2) * mm, "end": v(15.11, -255.75) * mm});
            skArc(sketch, "E90.trimOffspring", {"start": v(9.02, -243.84) * mm, "mid": v(31.87, -241.92) * mm, "end": v(54.43, -237.86) * mm});
            skArc(sketch, "E91.trimOffspring", {"start": v(-9.02, -249.94) * mm, "mid": v(0, -250.1) * mm, "end": v(9.02, -249.94) * mm});
            skLineSegment(sketch, "E92.trimOffspring", {"start": v(-9.02, -249.94) * mm, "end": v(-9.02, -243.84) * mm});
            skLineSegment(sketch, "E93.trimOffspring", {"start": v(9.02, -249.94) * mm, "end": v(9.02, -243.84) * mm});
            skArc(sketch, "E94.trimOffspring", {"start": v(15.11, -249.64) * mm, "mid": v(34.9, -247.65) * mm, "end": v(54.47, -244.1) * mm});
            skArc(sketch, "E95.1.0", {"start": v(232.3, 74.67) * mm, "mid": v(224.86, 94.76) * mm, "end": v(215.68, 114.11) * mm});
            skArc(sketch, "E95.1.1", {"start": v(237.68, 77.83) * mm, "mid": v(231.34, 95.04) * mm, "end": v(223.75, 111.73) * mm});
            skLineSegment(sketch, "E95.1.2", {"start": v(229.04, 114.79) * mm, "end": v(223.75, 111.73) * mm});
            skLineSegment(sketch, "E95.1.3", {"start": v(220.96, 117.16) * mm, "end": v(215.68, 114.11) * mm});
            skArc(sketch, "E95.1.4", {"start": v(220.96, 117.16) * mm, "mid": v(216.6, 125.05) * mm, "end": v(211.94, 132.78) * mm});
            skArc(sketch, "E95.1.5", {"start": v(229.04, 114.79) * mm, "mid": v(221.87, 128.1) * mm, "end": v(213.93, 140.96) * mm});
            skLineSegment(sketch, "E95.1.6", {"start": v(211.94, 132.78) * mm, "end": v(206.66, 129.73) * mm});
            skArc(sketch, "E95.1.7", {"start": v(206.66, 129.73) * mm, "mid": v(193.57, 148.55) * mm, "end": v(178.77, 166.07) * mm});
            skLineSegment(sketch, "E95.1.8", {"start": v(213.93, 140.96) * mm, "end": v(208.64, 137.91) * mm});
            skArc(sketch, "E95.1.9", {"start": v(208.64, 137.91) * mm, "mid": v(197.02, 154.05) * mm, "end": v(184.16, 169.22) * mm});
            skLineSegment(sketch, "E95.1.10", {"start": v(178.77, 166.07) * mm, "end": v(184.16, 169.22) * mm});
            skLineSegment(sketch, "E95.1.11", {"start": v(232.3, 74.67) * mm, "end": v(237.68, 77.83) * mm});
            skArc(sketch, "E95.2.0", {"start": v(-180.82, 163.84) * mm, "mid": v(-194.49, 147.35) * mm, "end": v(-206.66, 129.73) * mm});
            skArc(sketch, "E95.2.1", {"start": v(-186.24, 166.93) * mm, "mid": v(-197.97, 152.83) * mm, "end": v(-208.64, 137.91) * mm});
            skLineSegment(sketch, "E95.2.2", {"start": v(-213.93, 140.96) * mm, "end": v(-208.64, 137.91) * mm});
            skLineSegment(sketch, "E95.2.3", {"start": v(-211.94, 132.78) * mm, "end": v(-206.66, 129.73) * mm});
            skArc(sketch, "E95.2.4", {"start": v(-211.94, 132.78) * mm, "mid": v(-216.6, 125.05) * mm, "end": v(-220.96, 117.16) * mm});
            skArc(sketch, "E95.2.5", {"start": v(-213.93, 140.96) * mm, "mid": v(-221.87, 128.1) * mm, "end": v(-229.04, 114.79) * mm});
            skLineSegment(sketch, "E95.2.6", {"start": v(-220.96, 117.16) * mm, "end": v(-215.68, 114.11) * mm});
            skArc(sketch, "E95.2.7", {"start": v(-215.68, 114.11) * mm, "mid": v(-225.44, 93.36) * mm, "end": v(-233.2, 71.79) * mm});
            skLineSegment(sketch, "E95.2.8", {"start": v(-229.04, 114.79) * mm, "end": v(-223.75, 111.73) * mm});
            skArc(sketch, "E95.2.9", {"start": v(-223.75, 111.73) * mm, "mid": v(-231.93, 93.6) * mm, "end": v(-238.63, 74.87) * mm});
            skLineSegment(sketch, "E95.2.10", {"start": v(-233.2, 71.79) * mm, "end": v(-238.63, 74.87) * mm});
            skLineSegment(sketch, "E95.2.11", {"start": v(-180.82, 163.84) * mm, "end": v(-186.24, 166.93) * mm});
            skSolve(sketch);
        }
        {
            var Q0;
            Q0 = qSketchRegion(id + "F30", true);
            extrude(context, id + "F31", {"entities" : qUnion([Q0]), "operationType" : NewBodyOperationType.REMOVE, "oppositeDirection" : true, "depth" : 19.05 * mm});
        }
        {
            var Q0;
            Q0=qCreatedBy(makeId("Front.planeOp"),FACE);
            var sketch = newSketch(context, id + "F32", { "sketchPlane" : qUnion([Q0])});
            skLineSegment(sketch, "E96", {"start": v(-240.83, 0) * mm, "end": v(-240.83, -32.24) * mm});
            skArc(sketch, "E97", {"start": v(-240.83, 0) * mm, "mid": v(-238.93, 1.9) * mm, "end": v(-237.02, 0) * mm});
            skArc(sketch, "E98", {"start": v(237.02, 0) * mm, "mid": v(238.93, 1.9) * mm, "end": v(240.83, 0) * mm, "construction": true});
            skLineSegment(sketch, "E99", {"start": v(-237.02, 0) * mm, "end": v(-237.02, -32.24) * mm});
            skLineSegment(sketch, "E100", {"start": v(237.02, -10.92) * mm, "end": v(237.02, 0) * mm, "construction": true});
            skPoint(sketch, "E101.orphan", {"position": v(-237.02, -10.92) * mm});
            skLineSegment(sketch, "E102", {"start": v(-240.83, -32.24) * mm, "end": v(-237.02, -32.24) * mm});
            skSolve(sketch);
        }
        {
            var Q0;
            Q0=makeQuery(id+"F32.imprint","IMPRINT",FACE,{"disambiguationData":[TD([[makeQuery(id+"F32.imprint","IMPRINT",EDGE,{"derivedFrom":sQuery(id+"F32.wireOp",EDGE,"E96")}),1.0]])]});
            var Q1;
            Q1=sQuery(id+"F32.wireOp",EDGE,"E100");
            var Q2;
            Q2=sQuery(id+"F32.wireOp",EDGE,"E98");
            var Q3;
            Q3=makeQuery(id+"F26.boolean.opBoolean","SPLIT",FACE,{"disambiguationData":[TD([makeQuery(id+"F2.opRevolve","SWEPT_FACE",FACE,{"disambiguationData":[OSD([sQuery(id+"F0.wireOp",EDGE,"E1")])]}),makeQuery(id+"F2.opRevolve","SWEPT_FACE",FACE,{"disambiguationData":[OSD([sQuery(id+"F0.wireOp",EDGE,"E8.trimOffspring")])]}),makeQuery(id+"F26.opExtrude","SWEPT_FACE",FACE,{"disambiguationData":[OSD([sQuery(id+"F25.wireOp",EDGE,"E70")])]}),makeQuery(id+"F26.opExtrude","SWEPT_FACE",FACE,{"disambiguationData":[OSD([sQuery(id+"F25.wireOp",EDGE,"E71.2.1")])]})])],"derivedFrom":makeQuery(id+"F2.opRevolve","SWEPT_FACE",FACE,{"disambiguationData":[OSD([sQuery(id+"F0.wireOp",EDGE,"E3")])]})});
            revolve(context, id + "F33", {"operationType" : NewBodyOperationType.REMOVE, "entities" : qUnion([Q0]), "surfaceEntities" : qUnion([Q1, Q2]), "axis" : qUnion([Q3]), "revolveType" : RevolveType.FULL, "oppositeDirection" : true});
        }
    });
